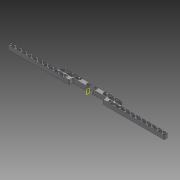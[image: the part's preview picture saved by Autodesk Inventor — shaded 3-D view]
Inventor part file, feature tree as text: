
AUTODESK INVENTOR PART (.ipt)
format: ipt  version: 2011 SP2 (Build 150309200, 309)  size: 1,117,696 bytes
history: native  units: mm
features: fillet x13, extrude x8, projected_geometry x8, sketch x6, plane x1, mirror x1
ambient origin geometry x8: Origin, YZ Plane, XZ Plane, XY Plane, X Axis, Y Axis, Z Axis, Center Point
feature tree (37):
  sketch  "Sketch1"  dims[d14=1.0mm d16=1.0mm]
  extrude  "Extrusion11"  Depth=1.0mm
  extrude  "Extrusion12"  Depth=1.0mm
  extrude  "Extrusion13"  Depth=16.580628mm
  extrude  "Extrusion14"  Depth=0.5mm
  extrude  "Extrusion15"  Depth=0.5mm
  extrude  "Extrusion16"  Depth=0.5mm
  fillet  "Fillet13"  Radius=0.5mm
  fillet  "Fillet14"  Radius=0.5mm
  fillet  "Fillet15"  Radius=0.5mm
  fillet  "Fillet16"  Radius=0.5mm
  fillet  "Fillet17"  Radius=0.5mm
  fillet  "Fillet18"  Radius=0.5mm
  fillet  "Fillet19"  Radius=0.5mm
  fillet  "Fillet20"  Radius=0.5mm
  fillet  "Fillet21"  Radius=0.5mm
  fillet  "Fillet22"  Radius=0.5mm
  fillet  "Fillet25"  Radius=0.5mm
  extrude  "Extrusion17"  Depth=0.5mm
  fillet  "Fillet26"  Radius=0.5mm
  extrude  "Extrusion18"  Depth=0.5mm
  fillet  "Fillet27"  Radius=0.5mm
  plane  "Work Plane2"
  mirror  "Mirror2"
  sketch  "Sketch11"  dims[d23=1.0mm d24=1.0mm]
  projected_geometry  "Projected Loop7"
  sketch  "Sketch12"  dims[d25=1.0mm d30=16.580628mm]
  projected_geometry  "Projected Loop8"
  projected_geometry  "Projected Loop9"
  sketch  "Sketch13"  dims[d32=1.0mm d62=0.5mm]
  sketch  "Sketch14"  dims[d64=0.5mm d65=0.5mm]
  sketch  "Sketch15"  dims[d66=0.5mm d68=0.5mm d69=0.5mm d70=0.5mm d71=0.5mm d72=0.5mm d73=0.5mm d74=0.5mm d75=0.5mm d76=0.5mm d77=0.5mm d78=0.5mm d79=0.5mm d80=0.5mm d81=0.5mm d82=0.5mm d83=0.5mm d84=0.5mm d85=0.5mm d86=0.5mm d87=0.5mm d88=0.5mm d89=0.5mm d90=0.5mm d91=0.5mm d92=0.5mm d93=0.5mm d94=0.5mm d95=0.5mm d96=0.5mm d97=0.5mm d98=0.5mm d99=0.5mm d100=0.5mm d101=0.5mm d102=0.5mm d103=0.5mm d104=0.5mm d106=0.5mm d107=0.5mm d108=0.5mm d109=0.5mm d115=14.209mm d116=3.912mm d120=5.45mm d121=3.75mm d122=1.875mm d124=2.725mm d126=3.060539mm d166=1.0mm d167=0.5mm d169=0.5mm d171=0.5mm d172=0.5mm d173=0.5mm d174=0.5mm d175=0.5mm d176=0.5mm d177=0.5mm d178=0.5mm d179=0.5mm d180=0.5mm d181=0.5mm d182=0.5mm d183=13.0mm d184=5.0mm d185=10.0mm d186=3.45mm d187=1.956mm d188=28.816511mm d189=34.516421mm d190=9.0mm d191=1.0mm d192=172.0mm d193=35.152794mm d194=10.0mm d195=0.0mm d196=10.0mm d197=0.0mm d198=5.384mm d199=0.0mm d200=10.0mm d201=8.0mm d202=0.0mm d203=14.835299mm d204=10.0mm d205=0.0mm d206=16.580628mm d207=10.0mm d208=0.0mm d209=1.0mm d210=1.0mm d211=0.5mm d212=1.75mm d213=0.2mm d214=1.0mm d215=0.5mm d216=0.5mm d217=0.5mm d218=1.0mm d221=2.25mm d222=10.0mm d223=0.0mm d224=0.75mm d225=10.0mm d226=0.0mm d227=0.5mm d228=-175.0mm]
  projected_geometry  "Projected Loop10"
  projected_geometry  "Projected Loop11"
  projected_geometry  "Projected Loop12"
  projected_geometry  "Projected Loop13"
  projected_geometry  "Projected Loop14"
